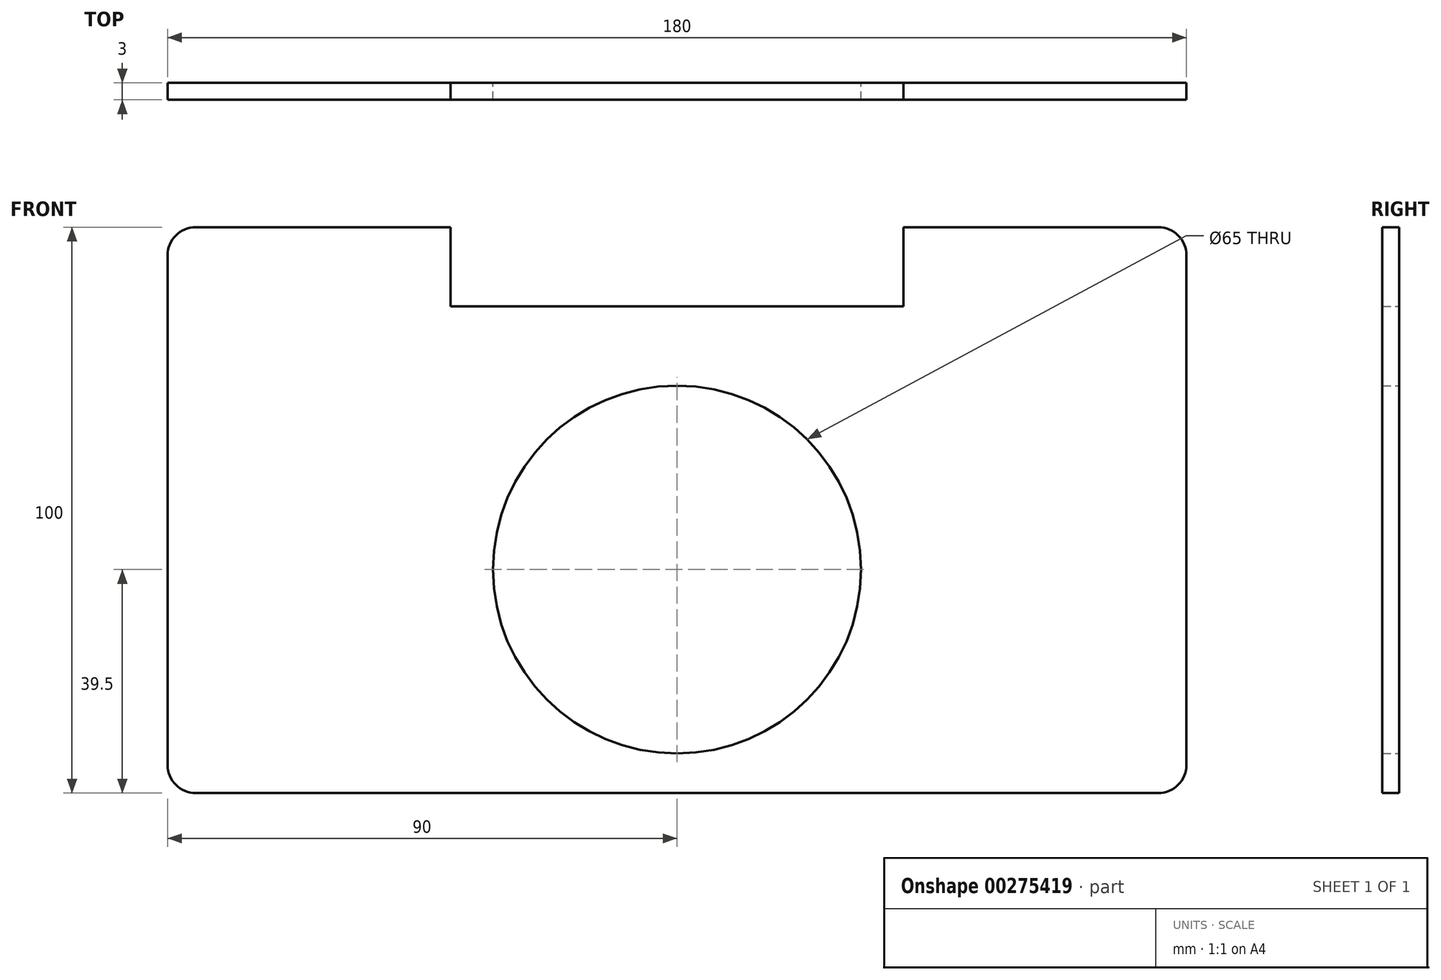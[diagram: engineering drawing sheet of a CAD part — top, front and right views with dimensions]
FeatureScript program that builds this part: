
annotation { "Feature Type Name" : "Feature", "Feature Type Description" : "" }
export const myFeature = defineFeature(function(context is Context, id is Id, definition is map)
    precondition{}
    {
        {
            var Q0;
            Q0=qCreatedBy(makeId("Front.planeOp"),FACE);
            var sketch = newSketch(context, id + "F0", { "sketchPlane" : qUnion([Q0])});
            skLineSegment(sketch, "E0.bottom", {"start": v(-85, 60.5) * mm, "end": v(85, 60.5) * mm});
            skLineSegment(sketch, "E0.top", {"start": v(-85, -39.5) * mm, "end": v(85, -39.5) * mm});
            skLineSegment(sketch, "E0.left", {"start": v(-90, 55.5) * mm, "end": v(-90, -34.5) * mm});
            skLineSegment(sketch, "E0.right", {"start": v(90, 55.5) * mm, "end": v(90, -34.5) * mm});
            skPoint(sketch, "E1.visualSharp", {"position": v(-90, -39.5) * mm});
            skArc(sketch, "E1.filletArc", {"start": v(-90, -34.5) * mm, "mid": v(-88.54, -38.04) * mm, "end": v(-85, -39.5) * mm});
            skPoint(sketch, "E2.visualSharp", {"position": v(-90, 60.5) * mm});
            skArc(sketch, "E2.filletArc", {"start": v(-85, 60.5) * mm, "mid": v(-88.54, 59.04) * mm, "end": v(-90, 55.5) * mm});
            skPoint(sketch, "E3.visualSharp", {"position": v(90, 60.5) * mm});
            skArc(sketch, "E3.filletArc", {"start": v(90, 55.5) * mm, "mid": v(88.54, 59.04) * mm, "end": v(85, 60.5) * mm});
            skPoint(sketch, "E4.visualSharp", {"position": v(90, -39.5) * mm});
            skArc(sketch, "E4.filletArc", {"start": v(85, -39.5) * mm, "mid": v(88.54, -38.04) * mm, "end": v(90, -34.5) * mm});
            skLineSegment(sketch, "E5.bottom", {"start": v(-40, 60.5) * mm, "end": v(40, 60.5) * mm});
            skLineSegment(sketch, "E5.top", {"start": v(-40, 46.5) * mm, "end": v(40, 46.5) * mm});
            skLineSegment(sketch, "E5.left", {"start": v(-40, 60.5) * mm, "end": v(-40, 46.5) * mm});
            skLineSegment(sketch, "E5.right", {"start": v(40, 60.5) * mm, "end": v(40, 46.5) * mm});
            skCircle(sketch, "E6", {"center": v(0, 0) * mm, "radius": 32.5 * mm});
            skSolve(sketch);
        }
        {
            var Q0;
            Q0=makeQuery(id+"F0.imprint","IMPRINT",FACE,{"disambiguationData":[TD([[makeQuery(id+"F0.imprint","IMPRINT",EDGE,{"derivedFrom":sQuery(id+"F0.wireOp",EDGE,"E0.bottom")}),-1.0]])]});
            extrude(context, id + "F1", {"entities" : qUnion([Q0]), "depth" : 3 * mm});
        }
        {
            var Q0;
            Q0 = qSketchRegion(id + "F0", true);
            extrude(context, id + "F2", {"entities" : qUnion([Q0]), "operationType" : NewBodyOperationType.REMOVE, "oppositeDirection" : true, "depth" : 20 * mm});
        }
    });
